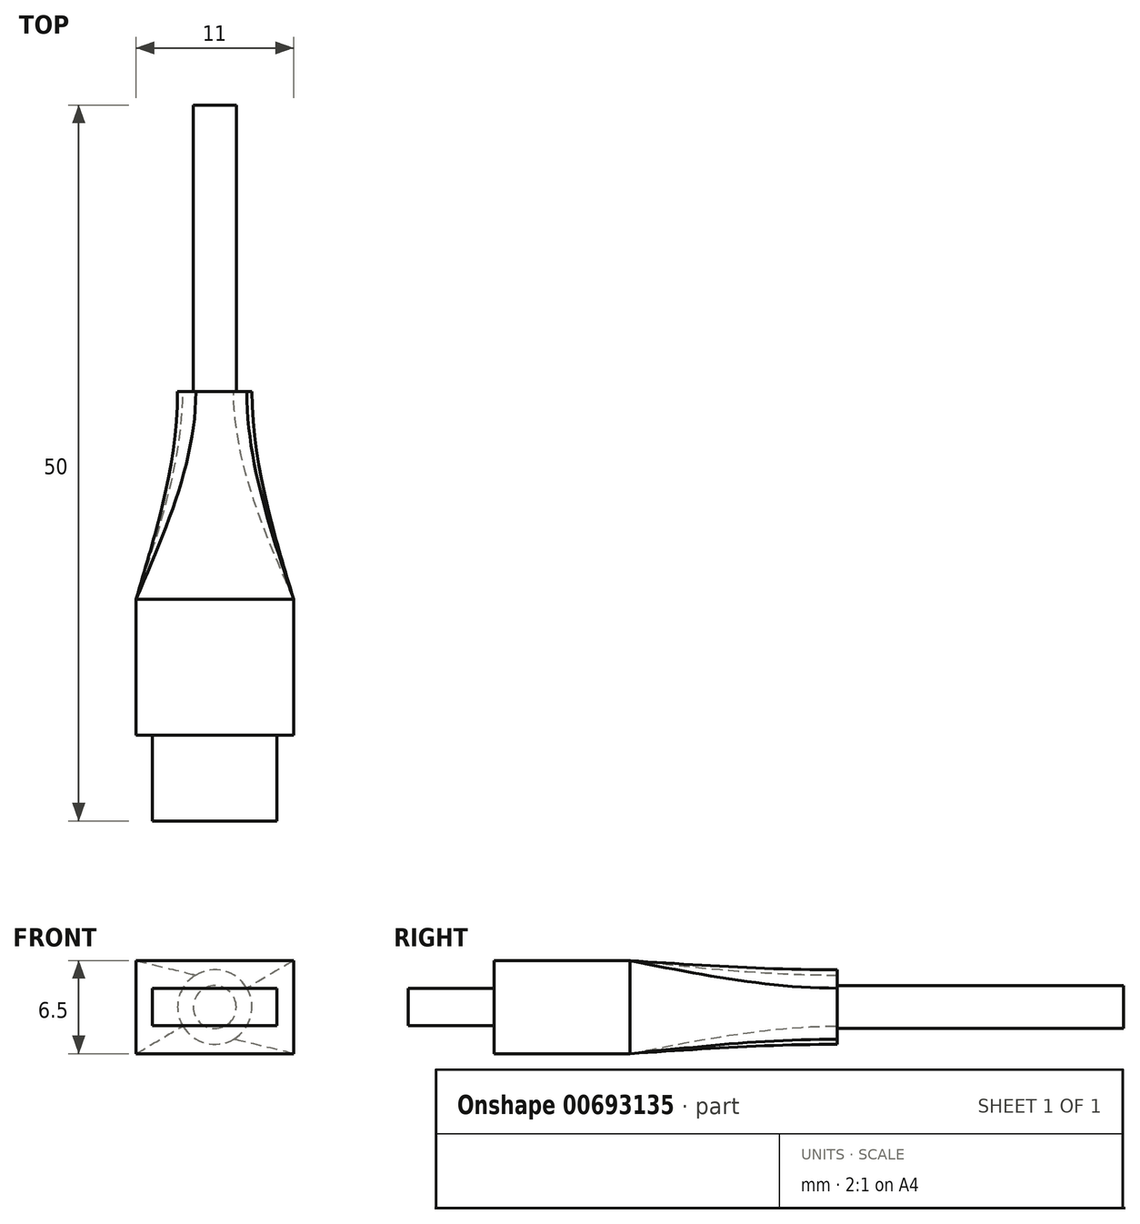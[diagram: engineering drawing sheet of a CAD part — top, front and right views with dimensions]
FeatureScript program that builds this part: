
annotation { "Feature Type Name" : "Feature", "Feature Type Description" : "" }
export const myFeature = defineFeature(function(context is Context, id is Id, definition is map)
    precondition{}
    {
        {
            var Q0;
            Q0=qCreatedBy(makeId("Front.planeOp"),FACE);
            var sketch = newSketch(context, id + "F0", { "sketchPlane" : qUnion([Q0])});
            skLineSegment(sketch, "E0", {"start": v(-6.95, 0) * mm, "end": v(7.26, 0) * mm, "construction": true});
            skLineSegment(sketch, "E1", {"start": v(0, -4.5) * mm, "end": v(0, 4.44) * mm, "construction": true});
            skLineSegment(sketch, "E2.bottom", {"start": v(4.35, 1.3) * mm, "end": v(-4.35, 1.3) * mm});
            skLineSegment(sketch, "E2.top", {"start": v(4.35, -1.3) * mm, "end": v(-4.35, -1.3) * mm});
            skLineSegment(sketch, "E2.left", {"start": v(4.35, 1.3) * mm, "end": v(4.35, -1.3) * mm});
            skLineSegment(sketch, "E2.right", {"start": v(-4.35, 1.3) * mm, "end": v(-4.35, -1.3) * mm});
            skPoint(sketch, "E2.middle", {"position": v(0, 0) * mm});
            skLineSegment(sketch, "E3.bottom", {"start": v(5.5, 3.25) * mm, "end": v(-5.5, 3.25) * mm});
            skLineSegment(sketch, "E3.top", {"start": v(5.5, -3.25) * mm, "end": v(-5.5, -3.25) * mm});
            skLineSegment(sketch, "E3.left", {"start": v(5.5, 3.25) * mm, "end": v(5.5, -3.25) * mm});
            skLineSegment(sketch, "E3.right", {"start": v(-5.5, 3.25) * mm, "end": v(-5.5, -3.25) * mm});
            skSolve(sketch);
        }
        {
            var Q0;
            Q0=makeQuery(id+"F0.imprint","IMPRINT",FACE,{"disambiguationData":[TD([[makeQuery(id+"F0.imprint","IMPRINT",EDGE,{"derivedFrom":sQuery(id+"F0.wireOp",EDGE,"E2.bottom")}),1.0]])]});
            extrude(context, id + "F1", {"entities" : qUnion([Q0]), "depth" : 6 * mm, "offsetDistance" : 25 * mm});
        }
        {
            var Q0;
            Q0=makeQuery(id+"F0.imprint","IMPRINT",FACE,{"disambiguationData":[TD([[makeQuery(id+"F0.imprint","IMPRINT",EDGE,{"derivedFrom":sQuery(id+"F0.wireOp",EDGE,"zUr5ZXLt-1GNU-IYbF-9KBn-N8l9aSGNwYDo.bottom")}),1.0]])]});
            var Q1;
            Q1=makeQuery(id+"F0.imprint","IMPRINT",FACE,{"disambiguationData":[TD([[makeQuery(id+"F0.imprint","IMPRINT",EDGE,{"derivedFrom":sQuery(id+"F0.wireOp",EDGE,"zUr5ZXLt-1GNU-IYbF-9KBn-N8l9aSGNwYDo.bottom")}),-1.0]])]});
            var Q2;
            Q2=makeQuery(id+"F0.imprint","IMPRINT",FACE,{"disambiguationData":[TD([[makeQuery(id+"F0.imprint","IMPRINT",EDGE,{"derivedFrom":sQuery(id+"F0.wireOp",EDGE,"E2.bottom")}),1.0]])]});
            var Q3;
            Q3=makeQuery(id+"F0.imprint","IMPRINT",FACE,{"disambiguationData":[TD([[makeQuery(id+"F0.imprint","IMPRINT",EDGE,{"derivedFrom":sQuery(id+"F0.wireOp",EDGE,"E2.bottom")}),-1.0]])]});
            extrude(context, id + "F2", {"entities" : qUnion([Q0, Q1, Q2, Q3]), "operationType" : NewBodyOperationType.ADD, "oppositeDirection" : true, "depth" : 9.5 * mm, "offsetDistance" : 25 * mm});
        }
        {
            var Q0;
            Q0=qCreatedBy(makeId("Front.planeOp"),FACE);
            cPlane(context, id + "F3", {"entities" : qUnion([Q0]), "cplaneType" : CPlaneType.OFFSET, "offset" : 24 * mm, "oppositeDirection" : true, "width" : 150 * mm, "height" : 150 * mm});
        }
        {
            var Q0;
            Q0=qCreatedBy(id+"F3.planeOp",FACE);
            var sketch = newSketch(context, id + "F4", { "sketchPlane" : qUnion([Q0])});
            skCircle(sketch, "E4", {"center": v(0, 0) * mm, "radius": 1.5 * mm});
            skSolve(sketch);
        }
        {
            var Q0;
            Q0=qCreatedBy(id+"F3.planeOp",FACE);
            var sketch = newSketch(context, id + "F5", { "sketchPlane" : qUnion([Q0])});
            skCircle(sketch, "E5", {"center": v(0, 0) * mm, "radius": 2.6 * mm});
            skSolve(sketch);
        }
        {
            var Q0;
            Q0=qCreatedBy(makeId("Top.planeOp"),FACE);
            var sketch = newSketch(context, id + "F6", { "sketchPlane" : qUnion([Q0])});
            skLineSegment(sketch, "E6", {"start": v(14.97, 9.5) * mm, "end": v(-15.87, 9.5) * mm, "construction": true});
            skLineSegment(sketch, "E7", {"start": v(15.68, 24) * mm, "end": v(-15.44, 24) * mm, "construction": true});
            skLineSegment(sketch, "E8", {"start": v(0, 29.8) * mm, "end": v(0, -6.4) * mm, "construction": true});
            skFitSpline(sketch, "E9", {"points": [v(5.5, 9.5) * mm, v(2.6, 24) * mm], "startDerivative": vector(-7.97, 12.99) * mm, "endDerivative": vector(0.1, 16.12) * mm});
            skFitSpline(sketch, "E10.MirrorCS", {"points": [v(-5.5, 9.5) * mm, v(-2.6, 24) * mm], "startDerivative": vector(7.97, 12.99) * mm, "endDerivative": vector(-0.1, 16.12) * mm});
            skSolve(sketch);
        }
        {
            var Q0;
            Q0=makeQuery(id+"F2.opExtrude","CAP_FACE",FACE,{"disambiguationData":[OSD([sQuery(id+"F0.wireOp",EDGE,"E3.bottom"),sQuery(id+"F0.wireOp",EDGE,"E3.top"),sQuery(id+"F0.wireOp",EDGE,"E3.left"),sQuery(id+"F0.wireOp",EDGE,"E3.right")])],"isStart":false});
            var Q1;
            Q1=makeQuery(id+"F5.imprint","IMPRINT",FACE,{"disambiguationData":[TD([[makeQuery(id+"F5.imprint","IMPRINT",EDGE,{"derivedFrom":sQuery(id+"F5.wireOp",EDGE,"E5")}),1.0]])]});
            var Q2;
            Q2=sQuery(id+"F6.wireOp",EDGE,"E9");
            var Q3;
            Q3=sQuery(id+"F6.wireOp",EDGE,"E10.MirrorCS");
            loft(context, id + "F7", {"endCondition" : LoftEndDerivativeType.NORMAL_TO_PROFILE, "endMagnitude" : 1, "sheetProfilesArray" : [{ "sheetProfileEntities" : qUnion([Q0]) }, { "sheetProfileEntities" : qUnion([Q1]) }], "guidesArray" : [{ "guideEntities" : qUnion([Q2]), "guideDerivativeType" : LoftGuideDerivativeType.DEFAULT, "guideDerivativeMagnitude" : 1 }, { "guideEntities" : qUnion([Q3]), "guideDerivativeType" : LoftGuideDerivativeType.DEFAULT, "guideDerivativeMagnitude" : 1 }]});
        }
        {
            var Q0;
            Q0=makeQuery(id+"F4.imprint","IMPRINT",FACE,{"disambiguationData":[TD([[makeQuery(id+"F4.imprint","IMPRINT",EDGE,{"derivedFrom":sQuery(id+"F4.wireOp",EDGE,"E4")}),1.0]])]});
            extrude(context, id + "F8", {"entities" : qUnion([Q0]), "oppositeDirection" : true, "depth" : 20 * mm, "offsetDistance" : 25 * mm});
        }
    });
